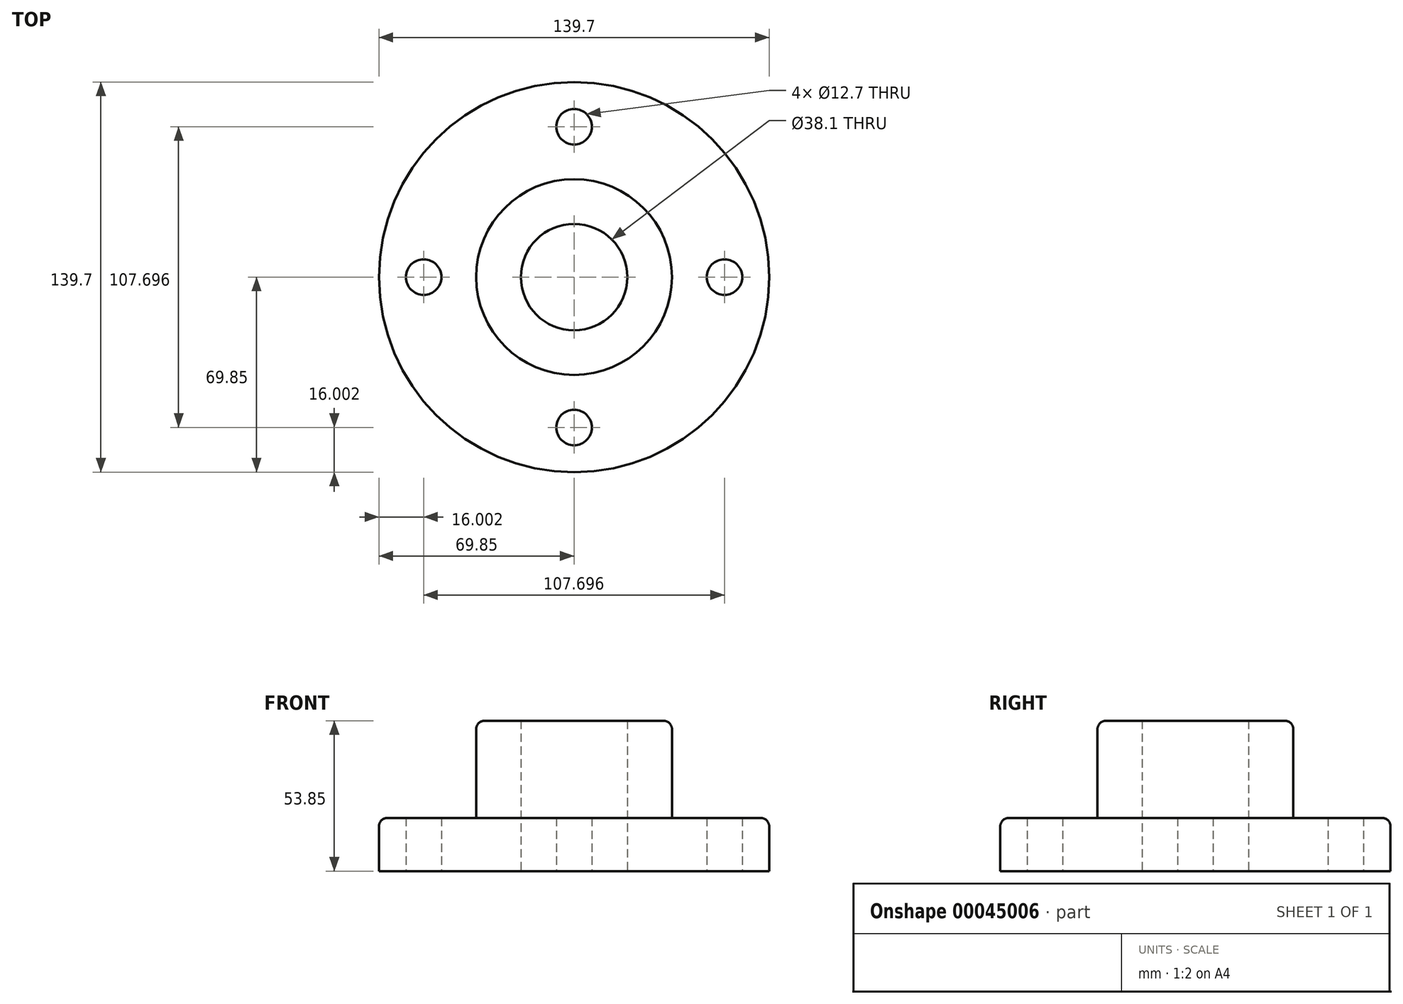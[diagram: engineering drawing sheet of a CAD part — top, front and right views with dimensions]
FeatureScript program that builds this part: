
annotation { "Feature Type Name" : "Feature", "Feature Type Description" : "" }
export const myFeature = defineFeature(function(context is Context, id is Id, definition is map)
    precondition{}
    {
        {
            var Q0;
            Q0=qCreatedBy(makeId("Top.planeOp"),FACE);
            var sketch = newSketch(context, id + "F0", { "sketchPlane" : qUnion([Q0])});
            skCircle(sketch, "E0", {"center": v(0, 0) * mm, "radius": 69.85 * mm});
            skCircle(sketch, "E1", {"center": v(0, 0) * mm, "radius": 19.05 * mm});
            skCircle(sketch, "E2", {"center": v(0, 53.85) * mm, "radius": 6.35 * mm});
            skCircle(sketch, "E3", {"center": v(0, 0) * mm, "radius": 53.85 * mm, "construction": true});
            skCircle(sketch, "E4.1.0", {"center": v(-53.85, 0) * mm, "radius": 6.35 * mm});
            skCircle(sketch, "E4.2.0", {"center": v(0, -53.85) * mm, "radius": 6.35 * mm});
            skCircle(sketch, "E4.3.0", {"center": v(53.85, 0) * mm, "radius": 6.35 * mm});
            skSolve(sketch);
        }
        {
            var Q0;
            Q0=makeQuery(id+"F0.imprint","IMPRINT",FACE,{"disambiguationData":[TD([[makeQuery(id+"F0.imprint","IMPRINT",EDGE,{"derivedFrom":sQuery(id+"F0.wireOp",EDGE,"E0")}),1.0]])]});
            extrude(context, id + "F1", {"entities" : qUnion([Q0]), "depth" : 19.05 * mm});
        }
        {
            var Q0;
            Q0=makeQuery(id+"F1.opExtrude","CAP_FACE",FACE,{"disambiguationData":[OSD([sQuery(id+"F0.wireOp",EDGE,"E0"),sQuery(id+"F0.wireOp",EDGE,"E1"),sQuery(id+"F0.wireOp",EDGE,"E2"),sQuery(id+"F0.wireOp",EDGE,"E4.1.0"),sQuery(id+"F0.wireOp",EDGE,"E4.2.0"),sQuery(id+"F0.wireOp",EDGE,"E4.3.0")])],"isStart":false});
            var sketch = newSketch(context, id + "F2", { "sketchPlane" : qUnion([Q0])});
            skCircle(sketch, "E5.0", {"center": v(0, 0) * mm, "radius": 19.05 * mm});
            skCircle(sketch, "E6", {"center": v(0, 0) * mm, "radius": 35.05 * mm});
            skSolve(sketch);
        }
        {
            var Q0;
            Q0 = qSketchRegion(id + "F2", true);
            extrude(context, id + "F3", {"entities" : qUnion([Q0]), "operationType" : NewBodyOperationType.ADD, "depth" : 34.8 * mm});
        }
        {
            var Q0;
            Q0=makeQuery(id+"F3.opExtrude","CAP_EDGE",EDGE,{"disambiguationData":[OSD([sQuery(id+"F2.wireOp",EDGE,"E6")])],"isStart":true});
            var Q1;
            Q1=makeQuery(id+"F3.opExtrude","CAP_EDGE",EDGE,{"disambiguationData":[OSD([sQuery(id+"F2.wireOp",EDGE,"E6")])],"isStart":false});
            var Q2;
            Q2=makeQuery(id+"F1.opExtrude","CAP_EDGE",EDGE,{"disambiguationData":[OSD([sQuery(id+"F0.wireOp",EDGE,"E0")])],"isStart":false});
            fillet(context, id + "F4", {"entities" : qUnion([Q0, Q1, Q2]), "radius" : 3.05 * mm, "tangentPropagation" : true, "allowEdgeOverflow" : false});
        }
    });
